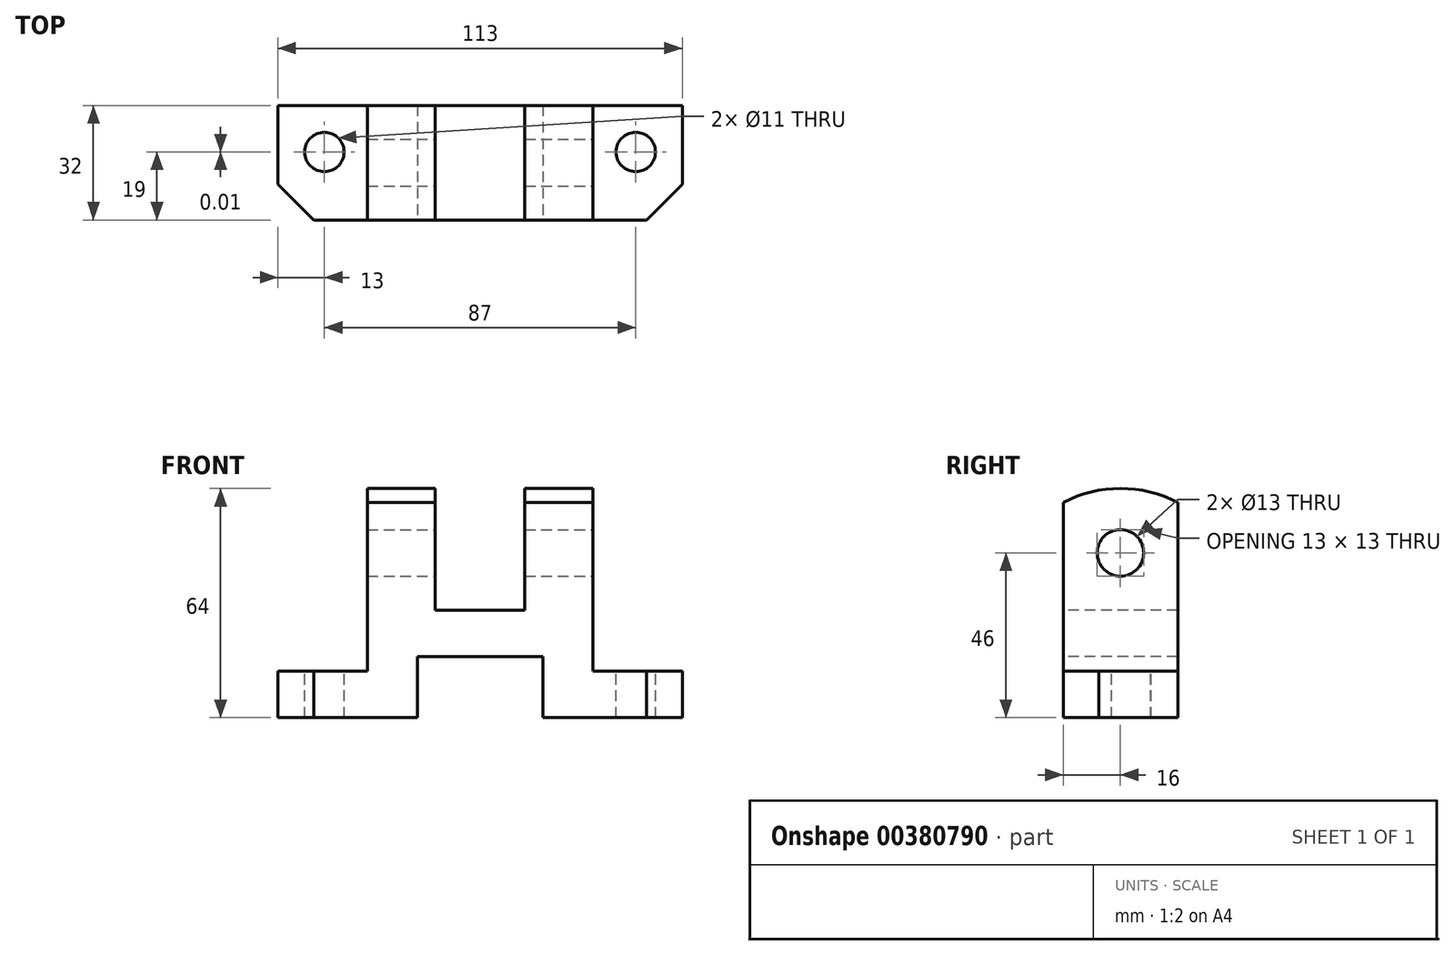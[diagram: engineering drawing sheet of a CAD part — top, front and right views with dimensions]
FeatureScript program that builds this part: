
annotation { "Feature Type Name" : "Feature", "Feature Type Description" : "" }
export const myFeature = defineFeature(function(context is Context, id is Id, definition is map)
    precondition{}
    {
        {
            var Q0;
            Q0=qCreatedBy(makeId("Top.planeOp"),FACE);
            var sketch = newSketch(context, id + "F0", { "sketchPlane" : qUnion([Q0])});
            skLineSegment(sketch, "E0.bottom", {"start": v(0, 0) * mm, "end": v(113, 0) * mm});
            skLineSegment(sketch, "E0.top", {"start": v(0, 32) * mm, "end": v(113, 32) * mm});
            skLineSegment(sketch, "E0.left", {"start": v(0, 0) * mm, "end": v(0, 32) * mm});
            skLineSegment(sketch, "E0.right", {"start": v(113, 0) * mm, "end": v(113, 32) * mm});
            skSolve(sketch);
        }
        {
            var Q0;
            Q0 = qSketchRegion(id + "F0", true);
            extrude(context, id + "F1", {"entities" : qUnion([Q0]), "depth" : 64 * mm});
        }
        {
            var Q0;
            Q0=makeQuery(id+"F1.opExtrude","SWEPT_FACE",FACE,{"disambiguationData":[OSD([sQuery(id+"F0.wireOp",EDGE,"E0.bottom")])]});
            var sketch = newSketch(context, id + "F2", { "sketchPlane" : qUnion([Q0])});
            skLineSegment(sketch, "E1.bottom", {"start": v(39, 0) * mm, "end": v(74, 0) * mm});
            skLineSegment(sketch, "E1.top", {"start": v(39, 17) * mm, "end": v(74, 17) * mm});
            skLineSegment(sketch, "E1.left", {"start": v(39, 0) * mm, "end": v(39, 17) * mm});
            skLineSegment(sketch, "E1.right", {"start": v(74, 0) * mm, "end": v(74, 17) * mm});
            skSolve(sketch);
        }
        {
            var Q0;
            Q0=makeQuery(id+"F2.imprint","IMPRINT",FACE,{"disambiguationData":[TD([[makeQuery(id+"F2.imprint","IMPRINT",EDGE,{"derivedFrom":sQuery(id+"F2.wireOp",EDGE,"E1.bottom")}),1.0]])]});
            extrude(context, id + "F3", {"entities" : qUnion([Q0]), "operationType" : NewBodyOperationType.REMOVE, "endBound" : BoundingType.THROUGH_ALL, "oppositeDirection" : true, "depth" : 25 * mm});
        }
        {
            var Q0;
            Q0=makeQuery(id+"F1.opExtrude","SWEPT_FACE",FACE,{"disambiguationData":[OSD([sQuery(id+"F0.wireOp",EDGE,"E0.bottom")])]});
            var sketch = newSketch(context, id + "F4", { "sketchPlane" : qUnion([Q0])});
            skLineSegment(sketch, "E2.bottom", {"start": v(44, 64) * mm, "end": v(69, 64) * mm});
            skLineSegment(sketch, "E2.top", {"start": v(44, 30) * mm, "end": v(69, 30) * mm});
            skLineSegment(sketch, "E2.left", {"start": v(44, 64) * mm, "end": v(44, 30) * mm});
            skLineSegment(sketch, "E2.right", {"start": v(69, 64) * mm, "end": v(69, 30) * mm});
            skSolve(sketch);
        }
        {
            var Q0;
            Q0 = qSketchRegion(id + "F4", true);
            extrude(context, id + "F5", {"entities" : qUnion([Q0]), "operationType" : NewBodyOperationType.REMOVE, "endBound" : BoundingType.THROUGH_ALL, "oppositeDirection" : true, "depth" : 25 * mm});
        }
        {
            var Q0;
            Q0=makeQuery(id+"F1.opExtrude","SWEPT_FACE",FACE,{"disambiguationData":[OSD([sQuery(id+"F0.wireOp",EDGE,"E0.bottom")])]});
            var sketch = newSketch(context, id + "F6", { "sketchPlane" : qUnion([Q0])});
            skLineSegment(sketch, "E3.bottom", {"start": v(0, 13) * mm, "end": v(25, 13) * mm});
            skLineSegment(sketch, "E3.top", {"start": v(0, 64) * mm, "end": v(25, 64) * mm});
            skLineSegment(sketch, "E3.left", {"start": v(0, 13) * mm, "end": v(0, 64) * mm});
            skLineSegment(sketch, "E3.right", {"start": v(25, 13) * mm, "end": v(25, 64) * mm});
            skLineSegment(sketch, "E4.bottom", {"start": v(113, 64) * mm, "end": v(88, 64) * mm});
            skLineSegment(sketch, "E4.top", {"start": v(113, 13) * mm, "end": v(88, 13) * mm});
            skLineSegment(sketch, "E4.left", {"start": v(113, 64) * mm, "end": v(113, 13) * mm});
            skLineSegment(sketch, "E4.right", {"start": v(88, 64) * mm, "end": v(88, 13) * mm});
            skSolve(sketch);
        }
        {
            var Q0;
            Q0 = qSketchRegion(id + "F6", true);
            extrude(context, id + "F7", {"entities" : qUnion([Q0]), "operationType" : NewBodyOperationType.REMOVE, "endBound" : BoundingType.THROUGH_ALL, "oppositeDirection" : true, "depth" : 25 * mm});
        }
        {
            var Q0;
            Q0=makeQuery(id+"F7.boolean.opBoolean","COPY",FACE,{"derivedFrom":makeQuery(id+"F7.opExtrude","SWEPT_FACE",FACE,{"disambiguationData":[OSD([sQuery(id+"F6.wireOp",EDGE,"E4.top")])]})});
            var sketch = newSketch(context, id + "F8", { "sketchPlane" : qUnion([Q0])});
            skCircle(sketch, "E5", {"center": v(100, 19) * mm, "radius": 5.5 * mm});
            skCircle(sketch, "E6", {"center": v(13, 19) * mm, "radius": 5.5 * mm});
            skSolve(sketch);
        }
        {
            var Q0;
            Q0 = qSketchRegion(id + "F8", true);
            extrude(context, id + "F9", {"entities" : qUnion([Q0]), "operationType" : NewBodyOperationType.REMOVE, "endBound" : BoundingType.THROUGH_ALL, "oppositeDirection" : true, "depth" : 25 * mm});
        }
        {
            var Q0;
            Q0=makeQuery(id+"F7.boolean.opBoolean","COPY",FACE,{"derivedFrom":makeQuery(id+"F7.opExtrude","SWEPT_FACE",FACE,{"disambiguationData":[OSD([sQuery(id+"F6.wireOp",EDGE,"E4.right")])]})});
            var sketch = newSketch(context, id + "F10", { "sketchPlane" : qUnion([Q0])});
            skCircle(sketch, "E7", {"center": v(16, 46) * mm, "radius": 6.5 * mm});
            skSolve(sketch);
        }
        {
            var Q0;
            Q0=makeQuery(id+"F10.imprint","IMPRINT",FACE,{"disambiguationData":[TD([[makeQuery(id+"F10.imprint","IMPRINT",EDGE,{"derivedFrom":sQuery(id+"F10.wireOp",EDGE,"E7")}),1.0]])]});
            extrude(context, id + "F11", {"entities" : qUnion([Q0]), "operationType" : NewBodyOperationType.REMOVE, "endBound" : BoundingType.THROUGH_ALL, "oppositeDirection" : true, "depth" : 25 * mm});
        }
        {
            var Q0;
            Q0=makeQuery(id+"F7.boolean.opBoolean","COPY",FACE,{"derivedFrom":makeQuery(id+"F7.opExtrude","SWEPT_FACE",FACE,{"disambiguationData":[OSD([sQuery(id+"F6.wireOp",EDGE,"E3.bottom")])]})});
            var sketch = newSketch(context, id + "F12", { "sketchPlane" : qUnion([Q0])});
            skLineSegment(sketch, "E8", {"start": v(0, 10) * mm, "end": v(10, 0) * mm});
            skSolve(sketch);
        }
        {
            var Q0;
            Q0=makeQuery(id+"F7.boolean.opBoolean","COPY",FACE,{"derivedFrom":makeQuery(id+"F7.opExtrude","SWEPT_FACE",FACE,{"disambiguationData":[OSD([sQuery(id+"F6.wireOp",EDGE,"E4.top")])]})});
            var sketch = newSketch(context, id + "F13", { "sketchPlane" : qUnion([Q0])});
            skLineSegment(sketch, "E9", {"start": v(113, 10) * mm, "end": v(103, 0) * mm});
            skSolve(sketch);
        }
        {
            var Q0;
            {var subQ0=sQuery(id+"F12.wireOp",EDGE,"E8");Q0=makeQuery(id+"F12.imprint","IMPRINT",FACE,{"disambiguationData":[TD([[makeQuery(id+"F12.imprint","IMPRINT",EDGE,{"derivedFrom":subQ0}),-1.0]])]});}
            var Q1;
            {var subQ0=sQuery(id+"F13.wireOp",EDGE,"E9");Q1=makeQuery(id+"F13.imprint","IMPRINT",FACE,{"disambiguationData":[TD([[makeQuery(id+"F13.imprint","IMPRINT",EDGE,{"derivedFrom":subQ0}),1.0]])]});}
            extrude(context, id + "F14", {"entities" : qUnion([Q0, Q1]), "operationType" : NewBodyOperationType.REMOVE, "endBound" : BoundingType.THROUGH_ALL, "oppositeDirection" : true, "depth" : 25 * mm});
        }
        {
            var Q0;
            Q0=makeQuery(id+"F7.boolean.opBoolean","COPY",FACE,{"derivedFrom":makeQuery(id+"F7.opExtrude","SWEPT_FACE",FACE,{"disambiguationData":[OSD([sQuery(id+"F6.wireOp",EDGE,"E4.right")])]})});
            var sketch = newSketch(context, id + "F15", { "sketchPlane" : qUnion([Q0])});
            skArc(sketch, "E10", {"start": v(32, 60.13) * mm, "mid": v(16, 64) * mm, "end": v(0, 60.13) * mm});
            skSolve(sketch);
        }
        {
            var Q0;
            {var subQ0=sQuery(id+"F15.wireOp",EDGE,"E10");var subQ1=sQuery(id+"F6.wireOp",EDGE,"E4.right");var subQ2=makeQuery(id+"F7.boolean.opBoolean","COPY",EDGE,{"derivedFrom":makeQuery(id+"F7.opExtrude","CAP_EDGE",EDGE,{"disambiguationData":[OSD([subQ1])],"isStart":true})});var subQ3=makeQuery(id+"F15.imprint","INTERSECT",VERTEX,{"derivedFrom":[subQ2,subQ0]});Q0=makeQuery(id+"F15.imprint","IMPRINT",FACE,{"disambiguationData":[TD([[makeQuery(id+"F15.imprint","IMPRINT",EDGE,{"disambiguationData":[TD([[subQ3,1.0]])],"derivedFrom":subQ0}),-1.0]])]});}
            var Q1;
            {var subQ0=sQuery(id+"F15.wireOp",EDGE,"E10");var subQ1=sQuery(id+"F6.wireOp",EDGE,"E4.right");var subQ2=makeQuery(id+"F7.boolean.opBoolean","INTERSECT",EDGE,{"derivedFrom":[makeQuery(id+"F1.opExtrude","SWEPT_FACE",FACE,{"disambiguationData":[OSD([sQuery(id+"F0.wireOp",EDGE,"E0.top")])]}),makeQuery(id+"F7.opExtrude","SWEPT_FACE",FACE,{"disambiguationData":[OSD([subQ1])]})]});var subQ3=makeQuery(id+"F15.imprint","INTERSECT",VERTEX,{"derivedFrom":[subQ2,subQ0]});Q1=makeQuery(id+"F15.imprint","IMPRINT",FACE,{"disambiguationData":[TD([[makeQuery(id+"F15.imprint","IMPRINT",EDGE,{"disambiguationData":[TD([[subQ3,-1.0]])],"derivedFrom":subQ0}),-1.0]])]});}
            extrude(context, id + "F16", {"entities" : qUnion([Q0, Q1]), "operationType" : NewBodyOperationType.REMOVE, "endBound" : BoundingType.THROUGH_ALL, "oppositeDirection" : true, "depth" : 25 * mm});
        }
    });
